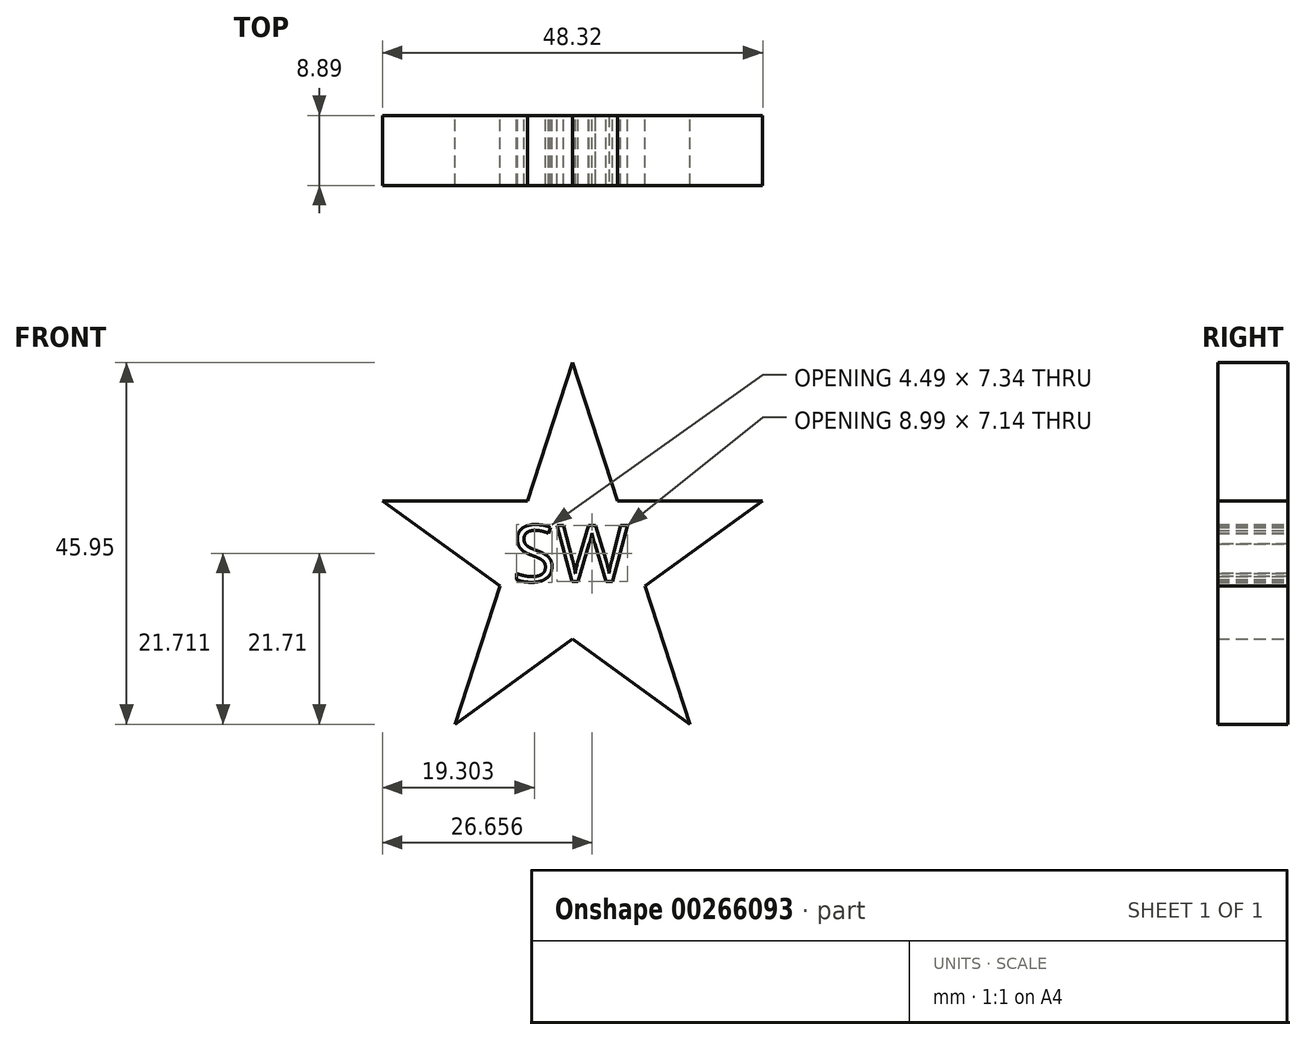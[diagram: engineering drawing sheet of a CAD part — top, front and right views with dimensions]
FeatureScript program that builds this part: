
annotation { "Feature Type Name" : "Feature", "Feature Type Description" : "" }
export const myFeature = defineFeature(function(context is Context, id is Id, definition is map)
    precondition{}
    {
        {
            var Q0;
            Q0=qCreatedBy(makeId("Front.planeOp"),FACE);
            var sketch = newSketch(context, id + "F0", { "sketchPlane" : qUnion([Q0])});
            skLineSegment(sketch, "E0", {"start": v(0, 25.4) * mm, "end": v(-14.93, -20.55) * mm});
            skLineSegment(sketch, "E1", {"start": v(-14.93, -20.55) * mm, "end": v(24.16, 7.85) * mm});
            skLineSegment(sketch, "E2", {"start": v(24.16, 7.85) * mm, "end": v(-24.16, 7.85) * mm});
            skLineSegment(sketch, "E3", {"start": v(-24.16, 7.85) * mm, "end": v(14.93, -20.55) * mm});
            skLineSegment(sketch, "E4", {"start": v(14.93, -20.55) * mm, "end": v(0, 25.4) * mm});
            skSolve(sketch);
        }
        {
            var Q0;
            {var subQ1=sQuery(id+"F0.wireOp",EDGE,"E0");var subQ5=sQuery(id+"F0.wireOp",EDGE,"E2");var subQ6=makeQuery(id+"F0.imprint","INTERSECT",VERTEX,{"derivedFrom":[subQ1,subQ5]});Q0=makeQuery(id+"F0.imprint","IMPRINT",FACE,{"disambiguationData":[TD([[makeQuery(id+"F0.imprint","IMPRINT",EDGE,{"disambiguationData":[TD([[subQ6,-1.0]])],"derivedFrom":subQ1}),1.0]])]});}
            var sketch = newSketch(context, id + "F1", { "sketchPlane" : qUnion([Q0])});
            skText(sketch, "E5", { "text": "SW", "fontName": "OpenSans-Regular.ttf"});
            const initialGuessF1  = {"E5": [-0.00762, -0.00241, 1, 0, 0.0072]};
            skSetInitialGuess(sketch, initialGuessF1);
            skSolve(sketch);
        }
        {
            var Q0;
            {var subQ0=sQuery(id+"F0.wireOp",EDGE,"E4");var subQ1=sQuery(id+"F0.wireOp",EDGE,"E0");var subQ2=makeQuery(id+"F0.imprint","INTERSECT",VERTEX,{"derivedFrom":[subQ1,subQ0]});Q0=makeQuery(id+"F0.imprint","IMPRINT",FACE,{"disambiguationData":[TD([[makeQuery(id+"F0.imprint","IMPRINT",EDGE,{"disambiguationData":[TD([[subQ2,-1.0]])],"derivedFrom":subQ1}),1.0]])]});}
            var Q1;
            {var subQ0=sQuery(id+"F0.wireOp",EDGE,"E2");var subQ1=sQuery(id+"F0.wireOp",EDGE,"E0");var subQ2=makeQuery(id+"F0.imprint","INTERSECT",VERTEX,{"derivedFrom":[subQ1,subQ0]});Q1=makeQuery(id+"F0.imprint","IMPRINT",FACE,{"disambiguationData":[TD([[makeQuery(id+"F0.imprint","IMPRINT",EDGE,{"disambiguationData":[TD([[subQ2,-1.0]])],"derivedFrom":subQ1}),-1.0]])]});}
            var Q2;
            {var subQ1=sQuery(id+"F0.wireOp",EDGE,"E0");var subQ5=sQuery(id+"F0.wireOp",EDGE,"E2");var subQ6=makeQuery(id+"F0.imprint","INTERSECT",VERTEX,{"derivedFrom":[subQ1,subQ5]});Q2=makeQuery(id+"F0.imprint","IMPRINT",FACE,{"disambiguationData":[TD([[makeQuery(id+"F0.imprint","IMPRINT",EDGE,{"disambiguationData":[TD([[subQ6,-1.0]])],"derivedFrom":subQ1}),1.0]])]});}
            var Q3;
            {var subQ0=sQuery(id+"F0.wireOp",EDGE,"E2");var subQ1=sQuery(id+"F0.wireOp",EDGE,"E1");var subQ2=makeQuery(id+"F0.imprint","INTERSECT",VERTEX,{"derivedFrom":[subQ1,subQ0]});Q3=makeQuery(id+"F0.imprint","IMPRINT",FACE,{"disambiguationData":[TD([[makeQuery(id+"F0.imprint","IMPRINT",EDGE,{"disambiguationData":[TD([[subQ2,1.0]])],"derivedFrom":subQ1}),1.0]])]});}
            var Q4;
            {var subQ0=sQuery(id+"F0.wireOp",EDGE,"E1");var subQ1=sQuery(id+"F0.wireOp",EDGE,"E0");var subQ2=makeQuery(id+"F0.imprint","INTERSECT",VERTEX,{"derivedFrom":[subQ1,subQ0]});Q4=makeQuery(id+"F0.imprint","IMPRINT",FACE,{"disambiguationData":[TD([[makeQuery(id+"F0.imprint","IMPRINT",EDGE,{"disambiguationData":[TD([[subQ2,1.0]])],"derivedFrom":subQ1}),1.0]])]});}
            var Q5;
            {var subQ0=sQuery(id+"F0.wireOp",EDGE,"E3");var subQ1=sQuery(id+"F0.wireOp",EDGE,"E1");var subQ2=makeQuery(id+"F0.imprint","INTERSECT",VERTEX,{"derivedFrom":[subQ1,subQ0]});Q5=makeQuery(id+"F0.imprint","IMPRINT",FACE,{"disambiguationData":[TD([[makeQuery(id+"F0.imprint","IMPRINT",EDGE,{"disambiguationData":[TD([[subQ2,-1.0]])],"derivedFrom":subQ1}),-1.0]])]});}
            extrude(context, id + "F2", {"entities" : qUnion([Q0, Q1, Q2, Q3, Q4, Q5]), "depth" : 8.9 * mm});
        }
        {
            var Q0;
            Q0 = qSketchRegion(id + "F1", true);
            var Q1;
            Q1 = qConstructionFilter(qBodyType(qCreatedBy(id + "F1" ,EDGE), BodyType.WIRE), ConstructionObject.NO);
            extrude(context, id + "F3", {"entities" : qUnion([Q0]), "operationType" : NewBodyOperationType.REMOVE, "surfaceEntities" : qUnion([Q1]), "depth" : 40.4 * mm});
        }
    });
